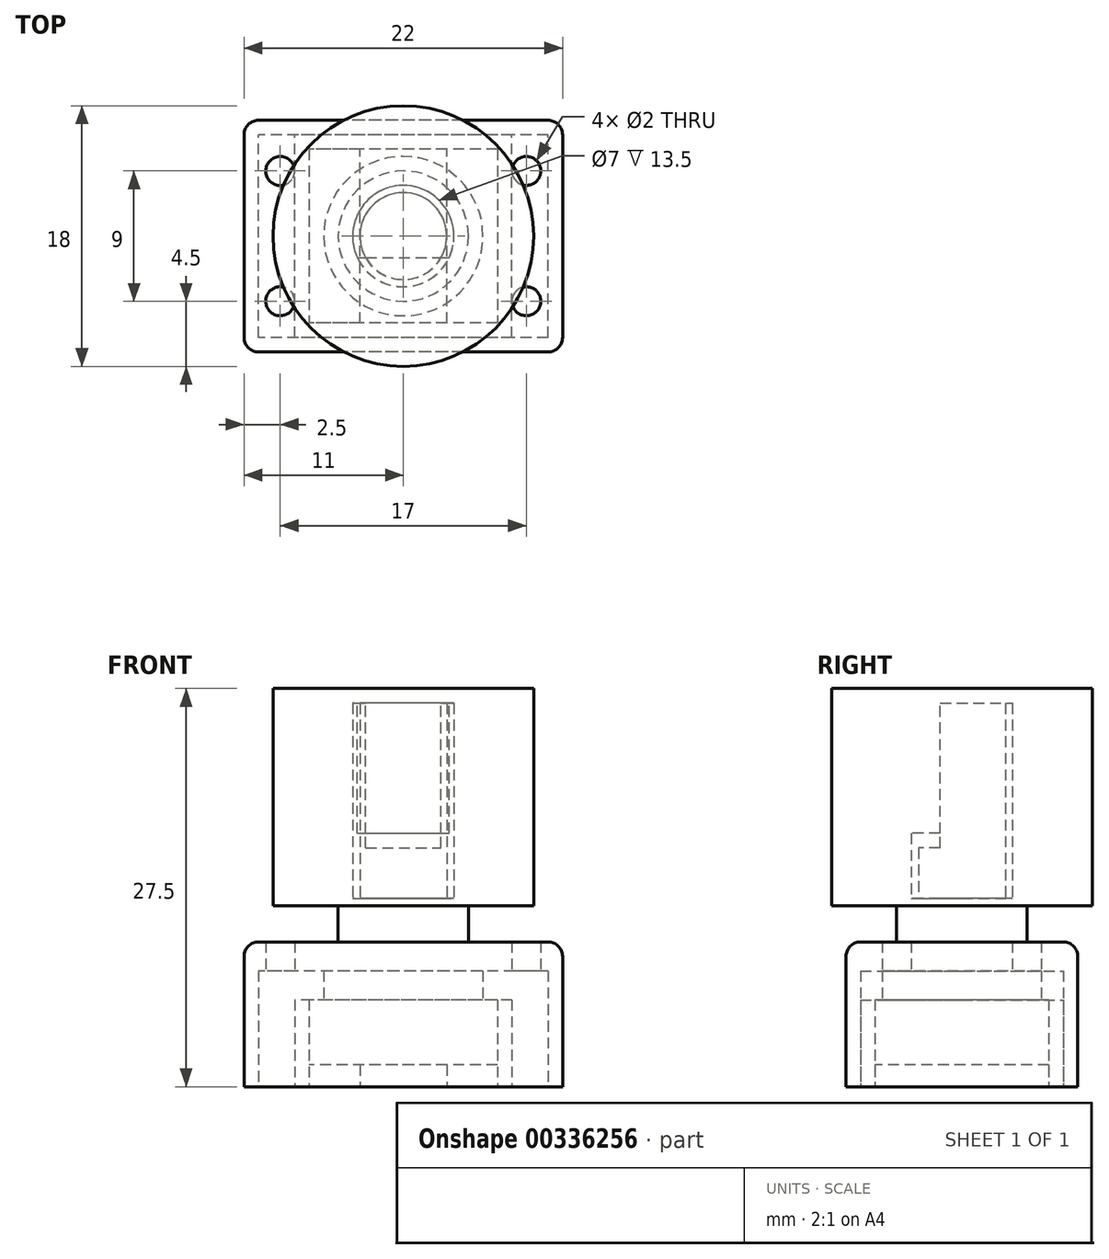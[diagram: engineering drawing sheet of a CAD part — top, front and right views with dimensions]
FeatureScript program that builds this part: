
annotation { "Feature Type Name" : "Feature", "Feature Type Description" : "" }
export const myFeature = defineFeature(function(context is Context, id is Id, definition is map)
    precondition{}
    {
        {
            var Q0;
            Q0=qCreatedBy(makeId("Top.planeOp"),FACE);
            var sketch = newSketch(context, id + "F0", { "sketchPlane" : qUnion([Q0])});
            skLineSegment(sketch, "E0.bottom", {"start": v(7.5, -7) * mm, "end": v(-7.5, -7) * mm});
            skLineSegment(sketch, "E0.top", {"start": v(7.5, 7) * mm, "end": v(-7.5, 7) * mm});
            skLineSegment(sketch, "E0.left", {"start": v(7.5, -7) * mm, "end": v(7.5, 7) * mm});
            skLineSegment(sketch, "E0.right", {"start": v(-7.5, -7) * mm, "end": v(-7.5, 7) * mm});
            skPoint(sketch, "E0.middle", {"position": v(0, 0) * mm});
            skLineSegment(sketch, "E1.bottom", {"start": v(6.5, -6) * mm, "end": v(-6.5, -6) * mm});
            skLineSegment(sketch, "E1.top", {"start": v(6.5, 6) * mm, "end": v(-6.5, 6) * mm});
            skLineSegment(sketch, "E1.left", {"start": v(6.5, -6) * mm, "end": v(6.5, 6) * mm});
            skLineSegment(sketch, "E1.right", {"start": v(-6.5, -6) * mm, "end": v(-6.5, 6) * mm});
            skLineSegment(sketch, "E2.bottom", {"start": v(-7.5, 7) * mm, "end": v(-10, 7) * mm, "construction": true});
            skLineSegment(sketch, "E2.top", {"start": v(-7.5, -7) * mm, "end": v(-10, -7) * mm, "construction": true});
            skLineSegment(sketch, "E2.left", {"start": v(-7.5, 7) * mm, "end": v(-7.5, -7) * mm});
            skLineSegment(sketch, "E2.right", {"start": v(-10, 7) * mm, "end": v(-10, -7) * mm, "construction": true});
            skCircle(sketch, "E3", {"center": v(-8.5, 4.5) * mm, "radius": 1 * mm, "construction": true});
            skCircle(sketch, "E4", {"center": v(-8.5, -4.5) * mm, "radius": 1 * mm, "construction": true});
            skLineSegment(sketch, "E5.bottom", {"start": v(7.5, 7) * mm, "end": v(10, 7) * mm, "construction": true});
            skLineSegment(sketch, "E5.top", {"start": v(7.5, -7) * mm, "end": v(10, -7) * mm, "construction": true});
            skLineSegment(sketch, "E5.left", {"start": v(7.5, 7) * mm, "end": v(7.5, -7) * mm});
            skLineSegment(sketch, "E5.right", {"start": v(10, 7) * mm, "end": v(10, -7) * mm, "construction": true});
            skCircle(sketch, "E6", {"center": v(8.5, 4.5) * mm, "radius": 1 * mm, "construction": true});
            skCircle(sketch, "E7", {"center": v(8.5, -4.5) * mm, "radius": 1 * mm, "construction": true});
            skSolve(sketch);
        }
        {
            var Q0;
            Q0 = qSketchRegion(id + "F0", true);
            extrude(context, id + "F1", {"entities" : qUnion([Q0]), "depth" : 6 * mm});
        }
        {
            var Q0;
            Q0=qCreatedBy(makeId("Top.planeOp"),FACE);
            var sketch = newSketch(context, id + "F2", { "sketchPlane" : qUnion([Q0])});
            skLineSegment(sketch, "E8.bottom", {"start": v(3, -6) * mm, "end": v(-3, -6) * mm});
            skLineSegment(sketch, "E8.top", {"start": v(3, 6) * mm, "end": v(-3, 6) * mm});
            skLineSegment(sketch, "E8.left", {"start": v(3, -6) * mm, "end": v(3, 6) * mm});
            skLineSegment(sketch, "E8.right", {"start": v(-3, -6) * mm, "end": v(-3, 6) * mm});
            skPoint(sketch, "E8.middle", {"position": v(0, 0) * mm});
            skSolve(sketch);
        }
        {
            var Q0;
            Q0 = qSketchRegion(id + "F2", true);
            extrude(context, id + "F3", {"entities" : qUnion([Q0]), "operationType" : NewBodyOperationType.ADD, "depth" : 1.5 * mm});
        }
        {
            var Q0;
            Q0=makeQuery(id+"F3.opExtrude","CAP_FACE",FACE,{"disambiguationData":[OSD([sQuery(id+"F2.wireOp",EDGE,"E8.bottom"),sQuery(id+"F2.wireOp",EDGE,"E8.top"),sQuery(id+"F2.wireOp",EDGE,"E8.left"),sQuery(id+"F2.wireOp",EDGE,"E8.right")])],"isStart":false});
            var sketch = newSketch(context, id + "F4", { "sketchPlane" : qUnion([Q0])});
            skLineSegment(sketch, "E9.bottom", {"start": v(6.5, 6) * mm, "end": v(-6.5, 6) * mm});
            skLineSegment(sketch, "E9.top", {"start": v(6.5, -6) * mm, "end": v(-6.5, -6) * mm});
            skLineSegment(sketch, "E9.left", {"start": v(6.5, 6) * mm, "end": v(6.5, -6) * mm});
            skLineSegment(sketch, "E9.right", {"start": v(-6.5, 6) * mm, "end": v(-6.5, -6) * mm});
            skPoint(sketch, "E9.middle", {"position": v(0, 0) * mm});
            skSolve(sketch);
        }
        {
            var Q0;
            Q0 = qSketchRegion(id + "F4", true);
            extrude(context, id + "F5", {"entities" : qUnion([Q0]), "depth" : 4.5 * mm});
        }
        {
            var Q0;
            Q0=makeQuery(id+"F5.opExtrude","CAP_FACE",FACE,{"disambiguationData":[OSD([sQuery(id+"F4.wireOp",EDGE,"E9.bottom"),sQuery(id+"F4.wireOp",EDGE,"E9.top"),sQuery(id+"F4.wireOp",EDGE,"E9.left"),sQuery(id+"F4.wireOp",EDGE,"E9.right")])],"isStart":false});
            var sketch = newSketch(context, id + "F6", { "sketchPlane" : qUnion([Q0])});
            skCircle(sketch, "E10", {"center": v(0, 0) * mm, "radius": 3.5 * mm});
            skSolve(sketch);
        }
        {
            var Q0;
            Q0 = qSketchRegion(id + "F6", true);
            extrude(context, id + "F7", {"entities" : qUnion([Q0]), "operationType" : NewBodyOperationType.ADD, "depth" : 7 * mm});
        }
        {
            var Q0;
            Q0=makeQuery(id+"F7.opExtrude","CAP_FACE",FACE,{"disambiguationData":[OSD([sQuery(id+"F6.wireOp",EDGE,"E10")])],"isStart":false});
            var sketch = newSketch(context, id + "F8", { "sketchPlane" : qUnion([Q0])});
            skCircle(sketch, "E11", {"center": v(0, 0) * mm, "radius": 3 * mm});
            skSolve(sketch);
        }
        {
            var Q0;
            Q0 = qSketchRegion(id + "F8", true);
            extrude(context, id + "F9", {"entities" : qUnion([Q0]), "operationType" : NewBodyOperationType.ADD, "depth" : 13.5 * mm});
        }
        {
            var Q0;
            Q0=makeQuery(id+"F9.opExtrude","CAP_FACE",FACE,{"disambiguationData":[OSD([sQuery(id+"F8.wireOp",EDGE,"E11")])],"isStart":false});
            var sketch = newSketch(context, id + "F10", { "sketchPlane" : qUnion([Q0])});
            skLineSegment(sketch, "E12", {"start": v(-4.96, -1.5) * mm, "end": v(5.12, -1.5) * mm, "construction": true});
            skArc(sketch, "E13", {"start": v(-2.6, -1.5) * mm, "mid": v(0, -3) * mm, "end": v(2.6, -1.5) * mm});
            skLineSegment(sketch, "E14", {"start": v(-2.6, -1.5) * mm, "end": v(2.6, -1.5) * mm});
            skSolve(sketch);
        }
        {
            var Q0;
            Q0 = qSketchRegion(id + "F10", true);
            extrude(context, id + "F11", {"entities" : qUnion([Q0]), "operationType" : NewBodyOperationType.REMOVE, "oppositeDirection" : true, "depth" : 10 * mm});
        }
        {
            var Q0;
            Q0=qCreatedBy(makeId("Top.planeOp"),FACE);
            var sketch = newSketch(context, id + "F12", { "sketchPlane" : qUnion([Q0])});
            skLineSegment(sketch, "E15.bottom", {"start": v(11, -8) * mm, "end": v(-11, -8) * mm});
            skLineSegment(sketch, "E15.top", {"start": v(11, 8) * mm, "end": v(-11, 8) * mm});
            skLineSegment(sketch, "E15.left", {"start": v(11, -8) * mm, "end": v(11, 8) * mm});
            skLineSegment(sketch, "E15.right", {"start": v(-11, -8) * mm, "end": v(-11, 8) * mm});
            skPoint(sketch, "E15.middle", {"position": v(0, 0) * mm});
            skLineSegment(sketch, "E16.bottom", {"start": v(10, -7) * mm, "end": v(-10, -7) * mm});
            skLineSegment(sketch, "E16.top", {"start": v(10, 7) * mm, "end": v(-10, 7) * mm});
            skLineSegment(sketch, "E16.left", {"start": v(10, -7) * mm, "end": v(10, 7) * mm});
            skLineSegment(sketch, "E16.right", {"start": v(-10, -7) * mm, "end": v(-10, 7) * mm});
            skSolve(sketch);
        }
        {
            var Q0;
            Q0 = qSketchRegion(id + "F12", true);
            extrude(context, id + "F13", {"entities" : qUnion([Q0]), "depth" : 8 * mm});
        }
        {
            var Q0;
            Q0=makeQuery(id+"F13.opExtrude","CAP_FACE",FACE,{"disambiguationData":[OSD([sQuery(id+"F12.wireOp",EDGE,"E15.bottom"),sQuery(id+"F12.wireOp",EDGE,"E15.top"),sQuery(id+"F12.wireOp",EDGE,"E15.left"),sQuery(id+"F12.wireOp",EDGE,"E15.right"),sQuery(id+"F12.wireOp",EDGE,"E16.bottom"),sQuery(id+"F12.wireOp",EDGE,"E16.top"),sQuery(id+"F12.wireOp",EDGE,"E16.left"),sQuery(id+"F12.wireOp",EDGE,"E16.right")])],"isStart":false});
            var sketch = newSketch(context, id + "F14", { "sketchPlane" : qUnion([Q0])});
            skLineSegment(sketch, "E17.bottom", {"start": v(-11, 8) * mm, "end": v(11, 8) * mm});
            skLineSegment(sketch, "E17.top", {"start": v(-11, -8) * mm, "end": v(11, -8) * mm});
            skLineSegment(sketch, "E17.left", {"start": v(-11, 8) * mm, "end": v(-11, -8) * mm});
            skLineSegment(sketch, "E17.right", {"start": v(11, 8) * mm, "end": v(11, -8) * mm});
            skCircle(sketch, "E18", {"center": v(0, 0) * mm, "radius": 4.5 * mm});
            skCircle(sketch, "E19", {"center": v(-8.5, 4.5) * mm, "radius": 1 * mm});
            skCircle(sketch, "E20", {"center": v(-8.5, -4.5) * mm, "radius": 1 * mm});
            skCircle(sketch, "E21", {"center": v(8.5, 4.5) * mm, "radius": 1 * mm});
            skCircle(sketch, "E22", {"center": v(8.5, -4.5) * mm, "radius": 1 * mm});
            skSolve(sketch);
        }
        {
            var Q0;
            Q0 = qSketchRegion(id + "F14", true);
            extrude(context, id + "F15", {"entities" : qUnion([Q0]), "operationType" : NewBodyOperationType.ADD, "depth" : 2 * mm});
        }
        {
            var Q0;
            Q0=makeQuery(id+"F15.boolean.opBoolean","MERGE",EDGE,{"derivedFrom":[makeQuery(id+"F13.opExtrude","SWEPT_EDGE",EDGE,{"disambiguationData":[OSD([sQuery(id+"F12.wireOp",EDGE,"E15.bottom"),sQuery(id+"F12.wireOp",EDGE,"E15.right")])]}),makeQuery(id+"F15.opExtrude","SWEPT_EDGE",EDGE,{"disambiguationData":[OSD([sQuery(id+"F14.wireOp",EDGE,"E17.top"),sQuery(id+"F14.wireOp",EDGE,"E17.left")])]})]});
            var Q1;
            Q1=makeQuery(id+"F15.boolean.opBoolean","MERGE",EDGE,{"derivedFrom":[makeQuery(id+"F13.opExtrude","SWEPT_EDGE",EDGE,{"disambiguationData":[OSD([sQuery(id+"F12.wireOp",EDGE,"E15.bottom"),sQuery(id+"F12.wireOp",EDGE,"E15.left")])]}),makeQuery(id+"F15.opExtrude","SWEPT_EDGE",EDGE,{"disambiguationData":[OSD([sQuery(id+"F14.wireOp",EDGE,"E17.top"),sQuery(id+"F14.wireOp",EDGE,"E17.right")])]})]});
            var Q2;
            Q2=makeQuery(id+"F15.boolean.opBoolean","MERGE",EDGE,{"derivedFrom":[makeQuery(id+"F13.opExtrude","SWEPT_EDGE",EDGE,{"disambiguationData":[OSD([sQuery(id+"F12.wireOp",EDGE,"E15.top"),sQuery(id+"F12.wireOp",EDGE,"E15.left")])]}),makeQuery(id+"F15.opExtrude","SWEPT_EDGE",EDGE,{"disambiguationData":[OSD([sQuery(id+"F14.wireOp",EDGE,"E17.bottom"),sQuery(id+"F14.wireOp",EDGE,"E17.right")])]})]});
            var Q3;
            Q3=makeQuery(id+"F15.boolean.opBoolean","MERGE",EDGE,{"derivedFrom":[makeQuery(id+"F13.opExtrude","SWEPT_EDGE",EDGE,{"disambiguationData":[OSD([sQuery(id+"F12.wireOp",EDGE,"E15.top"),sQuery(id+"F12.wireOp",EDGE,"E15.right")])]}),makeQuery(id+"F15.opExtrude","SWEPT_EDGE",EDGE,{"disambiguationData":[OSD([sQuery(id+"F14.wireOp",EDGE,"E17.bottom"),sQuery(id+"F14.wireOp",EDGE,"E17.left")])]})]});
            var Q4;
            Q4=makeQuery(id+"F15.opExtrude","CAP_EDGE",EDGE,{"disambiguationData":[OSD([sQuery(id+"F14.wireOp",EDGE,"E17.top")])],"isStart":false});
            var Q5;
            Q5=makeQuery(id+"F15.opExtrude","CAP_EDGE",EDGE,{"disambiguationData":[OSD([sQuery(id+"F14.wireOp",EDGE,"E17.bottom")])],"isStart":false});
            var Q6;
            Q6=makeQuery(id+"F15.opExtrude","CAP_EDGE",EDGE,{"disambiguationData":[OSD([sQuery(id+"F14.wireOp",EDGE,"E17.left")])],"isStart":false});
            var Q7;
            Q7=makeQuery(id+"F15.opExtrude","CAP_EDGE",EDGE,{"disambiguationData":[OSD([sQuery(id+"F14.wireOp",EDGE,"E17.right")])],"isStart":false});
            fillet(context, id + "F16", {"entities" : qUnion([Q0, Q1, Q2, Q3, Q4, Q5, Q6, Q7]), "radius" : 1 * mm, "tangentPropagation" : true, "allowEdgeOverflow" : false});
        }
        {
            var Q0;
            Q0=qCreatedBy(makeId("Top.planeOp"),FACE);
            cPlane(context, id + "F17", {"entities" : qUnion([Q0]), "cplaneType" : CPlaneType.OFFSET, "offset" : 6 * mm, "width" : 150 * mm, "height" : 150 * mm});
        }
        {
            var Q0;
            Q0=qCreatedBy(id+"F17.planeOp",FACE);
            var sketch = newSketch(context, id + "F18", { "sketchPlane" : qUnion([Q0])});
            skCircle(sketch, "E23", {"center": v(0, 0) * mm, "radius": 5.5 * mm});
            skCircle(sketch, "E24", {"center": v(0, 0) * mm, "radius": 3.5 * mm});
            skSolve(sketch);
        }
        {
            var Q0;
            Q0 = qSketchRegion(id + "F18", true);
            extrude(context, id + "F19", {"entities" : qUnion([Q0]), "depth" : 2 * mm});
        }
        {
            var Q0;
            Q0=makeQuery(id+"F19.opExtrude","CAP_FACE",FACE,{"disambiguationData":[OSD([sQuery(id+"F18.wireOp",EDGE,"E23"),sQuery(id+"F18.wireOp",EDGE,"E24")])],"isStart":false});
            var sketch = newSketch(context, id + "F20", { "sketchPlane" : qUnion([Q0])});
            skCircle(sketch, "E25", {"center": v(0, 0) * mm, "radius": 4.5 * mm});
            skCircle(sketch, "E26", {"center": v(0, 0) * mm, "radius": 3.5 * mm});
            skSolve(sketch);
        }
        {
            var Q0;
            Q0 = qSketchRegion(id + "F20", true);
            extrude(context, id + "F21", {"entities" : qUnion([Q0]), "operationType" : NewBodyOperationType.ADD, "depth" : 18.5 * mm});
        }
        {
            var Q0;
            Q0=makeQuery(id+"F21.opExtrude","CAP_FACE",FACE,{"disambiguationData":[OSD([sQuery(id+"F20.wireOp",EDGE,"E25"),sQuery(id+"F20.wireOp",EDGE,"E26")])],"isStart":false});
            var sketch = newSketch(context, id + "F22", { "sketchPlane" : qUnion([Q0])});
            skLineSegment(sketch, "E27", {"start": v(-3.16, -1.5) * mm, "end": v(3.16, -1.5) * mm});
            skArc(sketch, "E28", {"start": v(-3.16, -1.5) * mm, "mid": v(0, -3.5) * mm, "end": v(3.16, -1.5) * mm});
            skSolve(sketch);
        }
        {
            var Q0;
            Q0 = qSketchRegion(id + "F22", true);
            extrude(context, id + "F23", {"entities" : qUnion([Q0]), "operationType" : NewBodyOperationType.ADD, "oppositeDirection" : true, "depth" : 9 * mm});
        }
        {
            var Q0;
            Q0=makeQuery(id+"F23.boolean.opBoolean","MERGE",FACE,{"derivedFrom":[makeQuery(id+"F21.opExtrude","CAP_FACE",FACE,{"disambiguationData":[OSD([sQuery(id+"F20.wireOp",EDGE,"E25"),sQuery(id+"F20.wireOp",EDGE,"E26")])],"isStart":false}),makeQuery(id+"F23.opExtrude","CAP_FACE",FACE,{"disambiguationData":[OSD([sQuery(id+"F22.wireOp",EDGE,"E27"),sQuery(id+"F22.wireOp",EDGE,"E28")])],"isStart":true})]});
            var sketch = newSketch(context, id + "F24", { "sketchPlane" : qUnion([Q0])});
            skCircle(sketch, "E29", {"center": v(0, 0) * mm, "radius": 4.5 * mm});
            skSolve(sketch);
        }
        {
            var Q0;
            Q0 = qSketchRegion(id + "F24", true);
            extrude(context, id + "F25", {"entities" : qUnion([Q0]), "operationType" : NewBodyOperationType.ADD, "depth" : 1 * mm});
        }
        {
            var Q0;
            Q0=makeQuery(id+"F25.opExtrude","CAP_FACE",FACE,{"disambiguationData":[OSD([sQuery(id+"F24.wireOp",EDGE,"E29")])],"isStart":false});
            var sketch = newSketch(context, id + "F26", { "sketchPlane" : qUnion([Q0])});
            skCircle(sketch, "E30", {"center": v(0, 0) * mm, "radius": 3.5 * mm});
            skCircle(sketch, "E31", {"center": v(0, 0) * mm, "radius": 9 * mm});
            skSolve(sketch);
        }
        {
            var Q0;
            Q0 = qSketchRegion(id + "F26", true);
            extrude(context, id + "F27", {"entities" : qUnion([Q0]), "operationType" : NewBodyOperationType.ADD, "oppositeDirection" : true, "depth" : 15 * mm});
        }
    });
